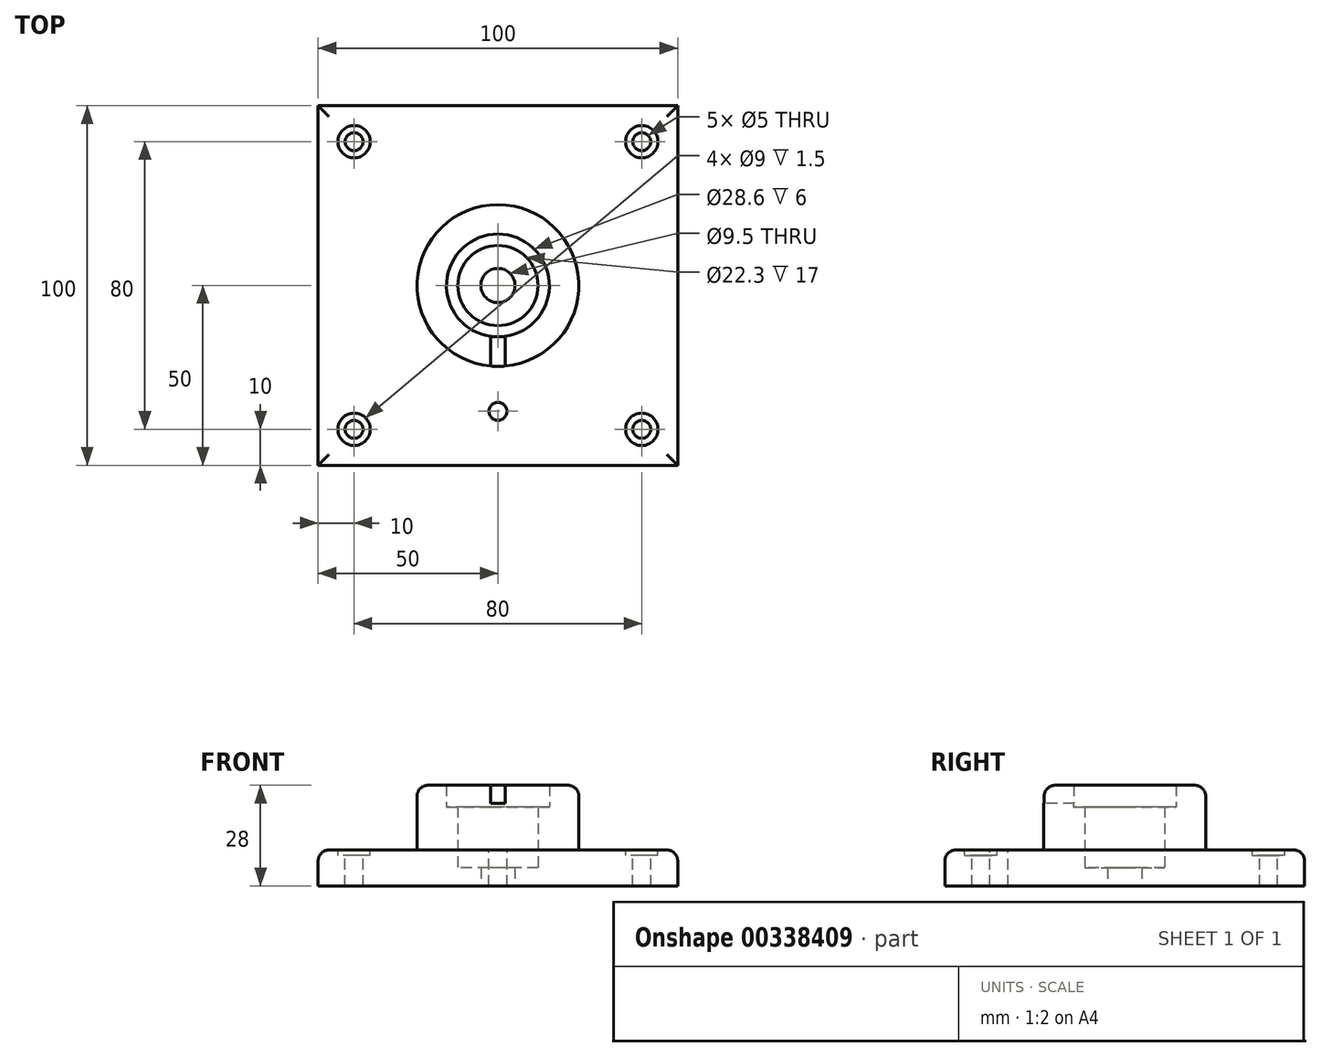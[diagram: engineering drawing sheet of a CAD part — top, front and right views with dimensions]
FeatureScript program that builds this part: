
annotation { "Feature Type Name" : "Feature", "Feature Type Description" : "" }
export const myFeature = defineFeature(function(context is Context, id is Id, definition is map)
    precondition{}
    {
        {
            var Q0;
            Q0=qCreatedBy(makeId("Top.planeOp"),FACE);
            var sketch = newSketch(context, id + "F0", { "sketchPlane" : qUnion([Q0])});
            skLineSegment(sketch, "E0.bottom", {"start": v(-50, 50) * mm, "end": v(50, 50) * mm});
            skLineSegment(sketch, "E0.top", {"start": v(-50, -50) * mm, "end": v(50, -50) * mm});
            skLineSegment(sketch, "E0.left", {"start": v(-50, 50) * mm, "end": v(-50, -50) * mm});
            skLineSegment(sketch, "E0.right", {"start": v(50, 50) * mm, "end": v(50, -50) * mm});
            skPoint(sketch, "E1", {"position": v(-40, 40) * mm});
            skPoint(sketch, "E2.MirrorP", {"position": v(40, 40) * mm});
            skPoint(sketch, "E3.MirrorP", {"position": v(-40, -40) * mm});
            skPoint(sketch, "E4.MirrorP", {"position": v(40, -40) * mm});
            skCircle(sketch, "E5", {"center": v(0, 0) * mm, "radius": 11.15 * mm});
            skCircle(sketch, "E6", {"center": v(0, 0) * mm, "radius": 14.3 * mm});
            skCircle(sketch, "E7", {"center": v(0, 0) * mm, "radius": 4.75 * mm});
            skCircle(sketch, "E8", {"center": v(0, 0) * mm, "radius": 22.5 * mm});
            skSolve(sketch);
        }
        {
            var Q0;
            Q0=makeQuery(id+"F0.imprint","IMPRINT",FACE,{"disambiguationData":[TD([[makeQuery(id+"F0.imprint","IMPRINT",EDGE,{"derivedFrom":sQuery(id+"F0.wireOp",EDGE,"E0.bottom")}),-1.0]])]});
            extrude(context, id + "F1", {"entities" : qUnion([Q0]), "depth" : 10 * mm});
        }
        {
            var Q0;
            Q0=makeQuery(id+"F0.imprint","IMPRINT",FACE,{"disambiguationData":[TD([[makeQuery(id+"F0.imprint","IMPRINT",EDGE,{"derivedFrom":sQuery(id+"F0.wireOp",EDGE,"E5")}),1.0]])]});
            extrude(context, id + "F2", {"entities" : qUnion([Q0]), "operationType" : NewBodyOperationType.ADD, "depth" : 5 * mm});
        }
        {
            var Q0;
            Q0=makeQuery(id+"F0.imprint","IMPRINT",FACE,{"disambiguationData":[TD([[makeQuery(id+"F0.imprint","IMPRINT",EDGE,{"derivedFrom":sQuery(id+"F0.wireOp",EDGE,"E5")}),-1.0]])]});
            extrude(context, id + "F3", {"entities" : qUnion([Q0]), "operationType" : NewBodyOperationType.ADD, "depth" : 22 * mm});
        }
        {
            var Q0;
            Q0=makeQuery(id+"F0.imprint","IMPRINT",FACE,{"disambiguationData":[TD([[makeQuery(id+"F0.imprint","IMPRINT",EDGE,{"derivedFrom":sQuery(id+"F0.wireOp",EDGE,"E6")}),-1.0]])]});
            extrude(context, id + "F4", {"entities" : qUnion([Q0]), "operationType" : NewBodyOperationType.ADD, "depth" : 28 * mm});
        }
        {
            var Q0;
            Q0=makeQuery(id+"F1.opExtrude","CAP_FACE",FACE,{"disambiguationData":[OSD([sQuery(id+"F0.wireOp",EDGE,"E0.bottom"),sQuery(id+"F0.wireOp",EDGE,"E0.top"),sQuery(id+"F0.wireOp",EDGE,"E0.left"),sQuery(id+"F0.wireOp",EDGE,"E0.right"),sQuery(id+"F0.wireOp",EDGE,"E8")])],"isStart":false});
            var sketch = newSketch(context, id + "F5", { "sketchPlane" : qUnion([Q0])});
            skPoint(sketch, "E9.0", {"position": v(-40, 40) * mm});
            skPoint(sketch, "E10.0", {"position": v(40, 40) * mm});
            skPoint(sketch, "E11.0", {"position": v(40, -40) * mm});
            skPoint(sketch, "E12.0", {"position": v(-40, -40) * mm});
            skCircle(sketch, "E13", {"center": v(0, -35) * mm, "radius": 2.5 * mm});
            skSolve(sketch);
        }
        {
            var Q0;
            Q0=sQuery(id+"F5.wireOp",VERTEX,"E9.0");
            var Q1;
            Q1=sQuery(id+"F5.wireOp",VERTEX,"E10.0");
            var Q2;
            Q2=sQuery(id+"F5.wireOp",VERTEX,"E11.0");
            var Q3;
            Q3=sQuery(id+"F5.wireOp",VERTEX,"E12.0");
            var Q4;
            Q4=makeQuery(id+"F1.opExtrude","SWEPT_BODY",BODY,{"disambiguationData":[OSD([sQuery(id+"F0.wireOp",EDGE,"E0.bottom"),sQuery(id+"F0.wireOp",EDGE,"E0.top"),sQuery(id+"F0.wireOp",EDGE,"E0.left"),sQuery(id+"F0.wireOp",EDGE,"E0.right"),sQuery(id+"F0.wireOp",EDGE,"E8")])]});
            hole(context, id + "F6", {"style" : HoleStyle.C_BORE, "endStyle" : HoleEndStyle.THROUGH, "holeDiameter" : 5 * mm, "cBoreDiameter" : 9 * mm, "cBoreDepth" : 1.5 * mm, "isTappedThrough" : true, "tappedDepth" : 12 * mm, "tapClearance" : 3, "locations" : qUnion([Q0, Q1, Q2, Q3]), "scope" : qUnion([Q4])});
        }
        {
            var Q0;
            Q0=makeQuery(id+"F1.opExtrude","CAP_EDGE",EDGE,{"disambiguationData":[OSD([sQuery(id+"F0.wireOp",EDGE,"E0.left")])],"isStart":false});
            var Q1;
            Q1=makeQuery(id+"F1.opExtrude","CAP_EDGE",EDGE,{"disambiguationData":[OSD([sQuery(id+"F0.wireOp",EDGE,"E0.bottom")])],"isStart":false});
            var Q2;
            Q2=makeQuery(id+"F1.opExtrude","CAP_EDGE",EDGE,{"disambiguationData":[OSD([sQuery(id+"F0.wireOp",EDGE,"E0.right")])],"isStart":false});
            var Q3;
            Q3=makeQuery(id+"F1.opExtrude","CAP_EDGE",EDGE,{"disambiguationData":[OSD([sQuery(id+"F0.wireOp",EDGE,"E0.top")])],"isStart":false});
            var Q4;
            Q4=makeQuery(id+"F1.opExtrude","CAP_EDGE",EDGE,{"disambiguationData":[OSD([sQuery(id+"F0.wireOp",EDGE,"E8")])],"isStart":false});
            var Q5;
            Q5=makeQuery(id+"F4.opExtrude","CAP_EDGE",EDGE,{"disambiguationData":[OSD([sQuery(id+"F0.wireOp",EDGE,"E8")])],"isStart":false});
            fillet(context, id + "F7", {"entities" : qUnion([Q0, Q1, Q2, Q3, Q4, Q5]), "radius" : 3 * mm, "tangentPropagation" : true, "allowEdgeOverflow" : false});
        }
        {
            var Q0;
            Q0=makeQuery(id+"F4.opExtrude","CAP_FACE",FACE,{"disambiguationData":[OSD([sQuery(id+"F0.wireOp",EDGE,"E6"),sQuery(id+"F0.wireOp",EDGE,"E8")])],"isStart":false});
            var sketch = newSketch(context, id + "F8", { "sketchPlane" : qUnion([Q0])});
            skLineSegment(sketch, "E14.bottom", {"start": v(-2, 0) * mm, "end": v(2, 0) * mm});
            skLineSegment(sketch, "E14.top", {"start": v(-2, -30) * mm, "end": v(2, -30) * mm});
            skLineSegment(sketch, "E14.left", {"start": v(-2, 0) * mm, "end": v(-2, -30) * mm});
            skLineSegment(sketch, "E14.right", {"start": v(2, 0) * mm, "end": v(2, -30) * mm});
            skSolve(sketch);
        }
        {
            var Q0;
            Q0 = qSketchRegion(id + "F8", true);
            extrude(context, id + "F9", {"entities" : qUnion([Q0]), "operationType" : NewBodyOperationType.REMOVE, "oppositeDirection" : true, "depth" : 5 * mm});
        }
        {
            var Q0;
            Q0=makeQuery(id+"F5.imprint","IMPRINT",FACE,{"disambiguationData":[TD([[makeQuery(id+"F5.imprint","IMPRINT",EDGE,{"derivedFrom":sQuery(id+"F5.wireOp",EDGE,"E13")}),1.0]])]});
            extrude(context, id + "F10", {"entities" : qUnion([Q0]), "operationType" : NewBodyOperationType.REMOVE, "endBound" : BoundingType.THROUGH_ALL, "oppositeDirection" : true, "depth" : 25 * mm});
        }
    });
